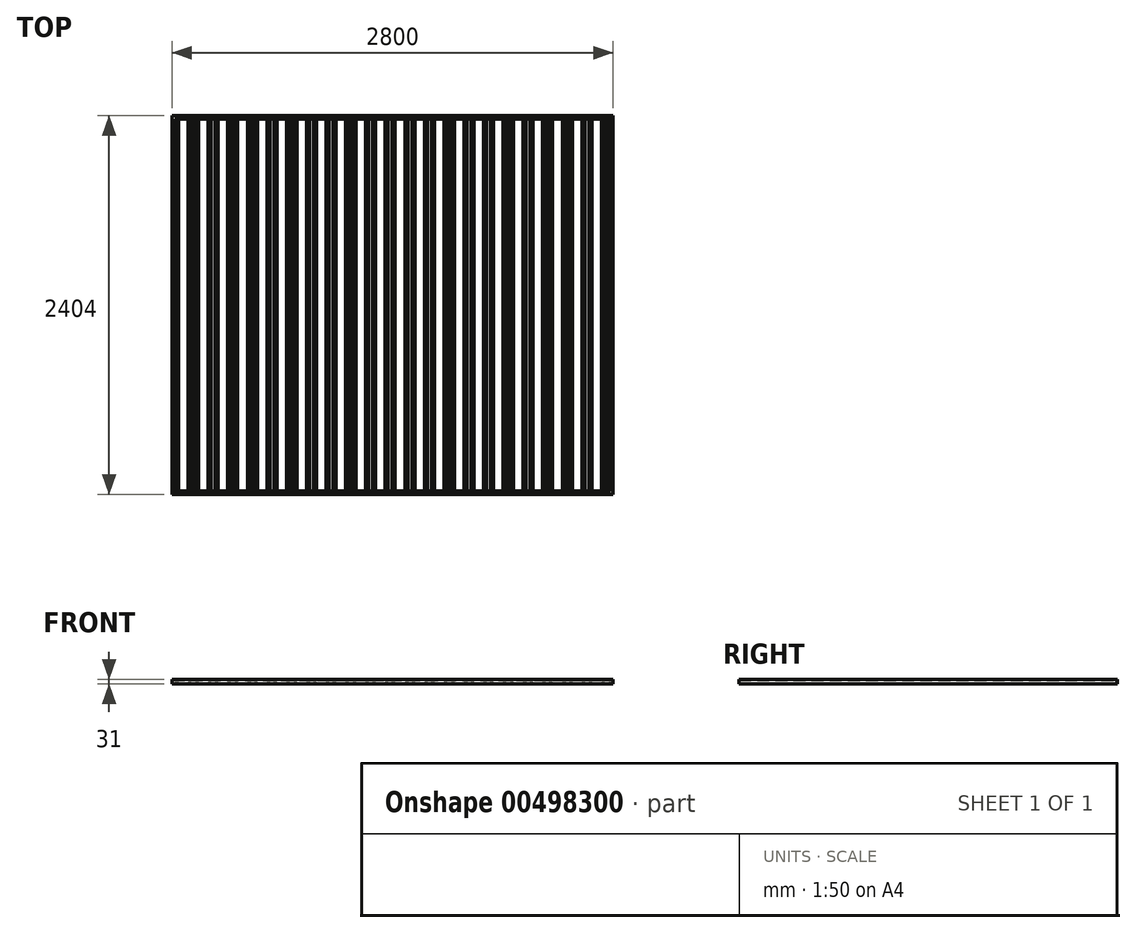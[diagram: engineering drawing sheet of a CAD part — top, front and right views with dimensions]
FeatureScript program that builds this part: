
annotation { "Feature Type Name" : "Feature", "Feature Type Description" : "" }
export const myFeature = defineFeature(function(context is Context, id is Id, definition is map)
    precondition{}
    {
        {
            var Q0;
            Q0=qCreatedBy(makeId("Front.planeOp"),FACE);
            var sketch = newSketch(context, id + "F0", { "sketchPlane" : qUnion([Q0])});
            skLineSegment(sketch, "E0", {"start": v(-64.81, 6.86) * mm, "end": v(-44.81, 6.86) * mm});
            skLineSegment(sketch, "E1", {"start": v(-44.81, 6.86) * mm, "end": v(-24.81, -13.14) * mm});
            skLineSegment(sketch, "E2", {"start": v(-24.81, -13.14) * mm, "end": v(40.19, -13.14) * mm});
            skLineSegment(sketch, "E3", {"start": v(40.19, -13.14) * mm, "end": v(60.19, 6.86) * mm});
            skLineSegment(sketch, "E4", {"start": v(60.19, 6.86) * mm, "end": v(80.19, 6.86) * mm});
            skLineSegment(sketch, "E5", {"start": v(80.19, 6.86) * mm, "end": v(100.19, -13.14) * mm});
            skLineSegment(sketch, "E6.55", {"start": v(38.12, -8.14) * mm, "end": v(58.12, 11.86) * mm});
            skLineSegment(sketch, "E6.56", {"start": v(-22.74, -8.14) * mm, "end": v(38.12, -8.14) * mm});
            skLineSegment(sketch, "E6.57", {"start": v(-42.74, 11.86) * mm, "end": v(-22.74, -8.14) * mm});
            skLineSegment(sketch, "E6.58", {"start": v(-64.81, 11.86) * mm, "end": v(-42.74, 11.86) * mm});
            skLineSegment(sketch, "E6.59", {"start": v(58.12, 11.86) * mm, "end": v(82.26, 11.86) * mm});
            skLineSegment(sketch, "E6.60", {"start": v(82.26, 11.86) * mm, "end": v(102.26, -8.14) * mm});
            skLineSegment(sketch, "E7", {"start": v(-64.81, 11.86) * mm, "end": v(-64.81, 6.86) * mm});
            skLineSegment(sketch, "E8.1.0.0", {"start": v(102.26, -8.14) * mm, "end": v(163.12, -8.14) * mm});
            skLineSegment(sketch, "E8.1.0.1", {"start": v(100.19, -13.14) * mm, "end": v(165.19, -13.14) * mm});
            skLineSegment(sketch, "E8.1.0.2", {"start": v(163.12, -8.14) * mm, "end": v(183.12, 11.86) * mm});
            skLineSegment(sketch, "E8.1.0.3", {"start": v(165.19, -13.14) * mm, "end": v(185.19, 6.86) * mm});
            skLineSegment(sketch, "E8.1.0.4", {"start": v(183.12, 11.86) * mm, "end": v(207.26, 11.86) * mm});
            skLineSegment(sketch, "E8.1.0.5", {"start": v(185.19, 6.86) * mm, "end": v(205.19, 6.86) * mm});
            skLineSegment(sketch, "E8.1.0.6", {"start": v(207.26, 11.86) * mm, "end": v(227.26, -8.14) * mm});
            skLineSegment(sketch, "E8.1.0.7", {"start": v(205.19, 6.86) * mm, "end": v(225.19, -13.14) * mm});
            skLineSegment(sketch, "E8.2.0.0", {"start": v(227.26, -8.14) * mm, "end": v(288.12, -8.14) * mm});
            skLineSegment(sketch, "E8.2.0.1", {"start": v(225.19, -13.14) * mm, "end": v(290.19, -13.14) * mm});
            skLineSegment(sketch, "E8.2.0.2", {"start": v(288.12, -8.14) * mm, "end": v(308.12, 11.86) * mm});
            skLineSegment(sketch, "E8.2.0.3", {"start": v(290.19, -13.14) * mm, "end": v(310.19, 6.86) * mm});
            skLineSegment(sketch, "E8.2.0.4", {"start": v(308.12, 11.86) * mm, "end": v(332.26, 11.86) * mm});
            skLineSegment(sketch, "E8.2.0.5", {"start": v(310.19, 6.86) * mm, "end": v(330.19, 6.86) * mm});
            skLineSegment(sketch, "E8.2.0.6", {"start": v(332.26, 11.86) * mm, "end": v(352.26, -8.14) * mm});
            skLineSegment(sketch, "E8.2.0.7", {"start": v(330.19, 6.86) * mm, "end": v(350.19, -13.14) * mm});
            skLineSegment(sketch, "E8.3.0.0", {"start": v(352.26, -8.14) * mm, "end": v(413.12, -8.14) * mm});
            skLineSegment(sketch, "E8.3.0.1", {"start": v(350.19, -13.14) * mm, "end": v(415.19, -13.14) * mm});
            skLineSegment(sketch, "E8.3.0.2", {"start": v(413.12, -8.14) * mm, "end": v(433.12, 11.86) * mm});
            skLineSegment(sketch, "E8.3.0.3", {"start": v(415.19, -13.14) * mm, "end": v(435.19, 6.86) * mm});
            skLineSegment(sketch, "E8.3.0.4", {"start": v(433.12, 11.86) * mm, "end": v(457.26, 11.86) * mm});
            skLineSegment(sketch, "E8.3.0.5", {"start": v(435.19, 6.86) * mm, "end": v(455.19, 6.86) * mm});
            skLineSegment(sketch, "E8.3.0.6", {"start": v(457.26, 11.86) * mm, "end": v(477.26, -8.14) * mm});
            skLineSegment(sketch, "E8.3.0.7", {"start": v(455.19, 6.86) * mm, "end": v(475.19, -13.14) * mm});
            skLineSegment(sketch, "E8.4.0.0", {"start": v(477.26, -8.14) * mm, "end": v(538.12, -8.14) * mm});
            skLineSegment(sketch, "E8.4.0.1", {"start": v(475.19, -13.14) * mm, "end": v(540.19, -13.14) * mm});
            skLineSegment(sketch, "E8.4.0.2", {"start": v(538.12, -8.14) * mm, "end": v(558.12, 11.86) * mm});
            skLineSegment(sketch, "E8.4.0.3", {"start": v(540.19, -13.14) * mm, "end": v(560.19, 6.86) * mm});
            skLineSegment(sketch, "E8.4.0.4", {"start": v(558.12, 11.86) * mm, "end": v(582.26, 11.86) * mm});
            skLineSegment(sketch, "E8.4.0.5", {"start": v(560.19, 6.86) * mm, "end": v(580.19, 6.86) * mm});
            skLineSegment(sketch, "E8.4.0.6", {"start": v(582.26, 11.86) * mm, "end": v(602.26, -8.14) * mm});
            skLineSegment(sketch, "E8.4.0.7", {"start": v(580.19, 6.86) * mm, "end": v(600.19, -13.14) * mm});
            skLineSegment(sketch, "E8.5.0.0", {"start": v(602.26, -8.14) * mm, "end": v(663.12, -8.14) * mm});
            skLineSegment(sketch, "E8.5.0.1", {"start": v(600.19, -13.14) * mm, "end": v(665.19, -13.14) * mm});
            skLineSegment(sketch, "E8.5.0.2", {"start": v(663.12, -8.14) * mm, "end": v(683.12, 11.86) * mm});
            skLineSegment(sketch, "E8.5.0.3", {"start": v(665.19, -13.14) * mm, "end": v(685.19, 6.86) * mm});
            skLineSegment(sketch, "E8.5.0.4", {"start": v(683.12, 11.86) * mm, "end": v(707.26, 11.86) * mm});
            skLineSegment(sketch, "E8.5.0.5", {"start": v(685.19, 6.86) * mm, "end": v(705.19, 6.86) * mm});
            skLineSegment(sketch, "E8.5.0.6", {"start": v(707.26, 11.86) * mm, "end": v(727.26, -8.14) * mm});
            skLineSegment(sketch, "E8.5.0.7", {"start": v(705.19, 6.86) * mm, "end": v(725.19, -13.14) * mm});
            skLineSegment(sketch, "E8.6.0.0", {"start": v(727.26, -8.14) * mm, "end": v(788.12, -8.14) * mm});
            skLineSegment(sketch, "E8.6.0.1", {"start": v(725.19, -13.14) * mm, "end": v(790.19, -13.14) * mm});
            skLineSegment(sketch, "E8.6.0.2", {"start": v(788.12, -8.14) * mm, "end": v(808.12, 11.86) * mm});
            skLineSegment(sketch, "E8.6.0.3", {"start": v(790.19, -13.14) * mm, "end": v(810.19, 6.86) * mm});
            skLineSegment(sketch, "E8.6.0.4", {"start": v(808.12, 11.86) * mm, "end": v(832.26, 11.86) * mm});
            skLineSegment(sketch, "E8.6.0.5", {"start": v(810.19, 6.86) * mm, "end": v(830.19, 6.86) * mm});
            skLineSegment(sketch, "E8.6.0.6", {"start": v(832.26, 11.86) * mm, "end": v(852.26, -8.14) * mm});
            skLineSegment(sketch, "E8.6.0.7", {"start": v(830.19, 6.86) * mm, "end": v(850.19, -13.14) * mm});
            skLineSegment(sketch, "E8.7.0.0", {"start": v(852.26, -8.14) * mm, "end": v(913.12, -8.14) * mm});
            skLineSegment(sketch, "E8.7.0.1", {"start": v(850.19, -13.14) * mm, "end": v(915.19, -13.14) * mm});
            skLineSegment(sketch, "E8.7.0.2", {"start": v(913.12, -8.14) * mm, "end": v(933.12, 11.86) * mm});
            skLineSegment(sketch, "E8.7.0.3", {"start": v(915.19, -13.14) * mm, "end": v(935.19, 6.86) * mm});
            skLineSegment(sketch, "E8.7.0.4", {"start": v(933.12, 11.86) * mm, "end": v(957.26, 11.86) * mm});
            skLineSegment(sketch, "E8.7.0.5", {"start": v(935.19, 6.86) * mm, "end": v(955.19, 6.86) * mm});
            skLineSegment(sketch, "E8.7.0.6", {"start": v(957.26, 11.86) * mm, "end": v(977.26, -8.14) * mm});
            skLineSegment(sketch, "E8.7.0.7", {"start": v(955.19, 6.86) * mm, "end": v(975.19, -13.14) * mm});
            skLineSegment(sketch, "E8.8.0.0", {"start": v(977.26, -8.14) * mm, "end": v(1038.12, -8.14) * mm});
            skLineSegment(sketch, "E8.8.0.1", {"start": v(975.19, -13.14) * mm, "end": v(1040.19, -13.14) * mm});
            skLineSegment(sketch, "E8.8.0.2", {"start": v(1038.12, -8.14) * mm, "end": v(1058.12, 11.86) * mm});
            skLineSegment(sketch, "E8.8.0.3", {"start": v(1040.19, -13.14) * mm, "end": v(1060.19, 6.86) * mm});
            skLineSegment(sketch, "E8.8.0.4", {"start": v(1058.12, 11.86) * mm, "end": v(1082.26, 11.86) * mm});
            skLineSegment(sketch, "E8.8.0.5", {"start": v(1060.19, 6.86) * mm, "end": v(1080.19, 6.86) * mm});
            skLineSegment(sketch, "E8.8.0.6", {"start": v(1082.26, 11.86) * mm, "end": v(1102.26, -8.14) * mm});
            skLineSegment(sketch, "E8.8.0.7", {"start": v(1080.19, 6.86) * mm, "end": v(1100.19, -13.14) * mm});
            skLineSegment(sketch, "E8.9.0.0", {"start": v(1102.26, -8.14) * mm, "end": v(1163.12, -8.14) * mm});
            skLineSegment(sketch, "E8.9.0.1", {"start": v(1100.19, -13.14) * mm, "end": v(1165.19, -13.14) * mm});
            skLineSegment(sketch, "E8.9.0.2", {"start": v(1163.12, -8.14) * mm, "end": v(1183.12, 11.86) * mm});
            skLineSegment(sketch, "E8.9.0.3", {"start": v(1165.19, -13.14) * mm, "end": v(1185.19, 6.86) * mm});
            skLineSegment(sketch, "E8.9.0.4", {"start": v(1183.12, 11.86) * mm, "end": v(1207.26, 11.86) * mm});
            skLineSegment(sketch, "E8.9.0.5", {"start": v(1185.19, 6.86) * mm, "end": v(1205.19, 6.86) * mm});
            skLineSegment(sketch, "E8.9.0.6", {"start": v(1207.26, 11.86) * mm, "end": v(1227.26, -8.14) * mm});
            skLineSegment(sketch, "E8.9.0.7", {"start": v(1205.19, 6.86) * mm, "end": v(1225.19, -13.14) * mm});
            skLineSegment(sketch, "E8.10.0.0", {"start": v(1227.26, -8.14) * mm, "end": v(1288.12, -8.14) * mm});
            skLineSegment(sketch, "E8.10.0.1", {"start": v(1225.19, -13.14) * mm, "end": v(1290.19, -13.14) * mm});
            skLineSegment(sketch, "E8.10.0.2", {"start": v(1288.12, -8.14) * mm, "end": v(1308.12, 11.86) * mm});
            skLineSegment(sketch, "E8.10.0.3", {"start": v(1290.19, -13.14) * mm, "end": v(1310.19, 6.86) * mm});
            skLineSegment(sketch, "E8.10.0.4", {"start": v(1308.12, 11.86) * mm, "end": v(1332.26, 11.86) * mm});
            skLineSegment(sketch, "E8.10.0.5", {"start": v(1310.19, 6.86) * mm, "end": v(1330.19, 6.86) * mm});
            skLineSegment(sketch, "E8.10.0.6", {"start": v(1332.26, 11.86) * mm, "end": v(1352.26, -8.14) * mm});
            skLineSegment(sketch, "E8.10.0.7", {"start": v(1330.19, 6.86) * mm, "end": v(1350.19, -13.14) * mm});
            skLineSegment(sketch, "E8.11.0.0", {"start": v(1352.26, -8.14) * mm, "end": v(1413.12, -8.14) * mm});
            skLineSegment(sketch, "E8.11.0.1", {"start": v(1350.19, -13.14) * mm, "end": v(1415.19, -13.14) * mm});
            skLineSegment(sketch, "E8.11.0.2", {"start": v(1413.12, -8.14) * mm, "end": v(1433.12, 11.86) * mm});
            skLineSegment(sketch, "E8.11.0.3", {"start": v(1415.19, -13.14) * mm, "end": v(1435.19, 6.86) * mm});
            skLineSegment(sketch, "E8.11.0.4", {"start": v(1433.12, 11.86) * mm, "end": v(1457.26, 11.86) * mm});
            skLineSegment(sketch, "E8.11.0.5", {"start": v(1435.19, 6.86) * mm, "end": v(1455.19, 6.86) * mm});
            skLineSegment(sketch, "E8.11.0.6", {"start": v(1457.26, 11.86) * mm, "end": v(1477.26, -8.14) * mm});
            skLineSegment(sketch, "E8.11.0.7", {"start": v(1455.19, 6.86) * mm, "end": v(1475.19, -13.14) * mm});
            skLineSegment(sketch, "E8.12.0.0", {"start": v(1477.26, -8.14) * mm, "end": v(1538.12, -8.14) * mm});
            skLineSegment(sketch, "E8.12.0.1", {"start": v(1475.19, -13.14) * mm, "end": v(1540.19, -13.14) * mm});
            skLineSegment(sketch, "E8.12.0.2", {"start": v(1538.12, -8.14) * mm, "end": v(1558.12, 11.86) * mm});
            skLineSegment(sketch, "E8.12.0.3", {"start": v(1540.19, -13.14) * mm, "end": v(1560.19, 6.86) * mm});
            skLineSegment(sketch, "E8.12.0.4", {"start": v(1558.12, 11.86) * mm, "end": v(1582.26, 11.86) * mm});
            skLineSegment(sketch, "E8.12.0.5", {"start": v(1560.19, 6.86) * mm, "end": v(1580.19, 6.86) * mm});
            skLineSegment(sketch, "E8.12.0.6", {"start": v(1582.26, 11.86) * mm, "end": v(1602.26, -8.14) * mm});
            skLineSegment(sketch, "E8.12.0.7", {"start": v(1580.19, 6.86) * mm, "end": v(1600.19, -13.14) * mm});
            skLineSegment(sketch, "E8.13.0.0", {"start": v(1602.26, -8.14) * mm, "end": v(1663.12, -8.14) * mm});
            skLineSegment(sketch, "E8.13.0.1", {"start": v(1600.19, -13.14) * mm, "end": v(1665.19, -13.14) * mm});
            skLineSegment(sketch, "E8.13.0.2", {"start": v(1663.12, -8.14) * mm, "end": v(1683.12, 11.86) * mm});
            skLineSegment(sketch, "E8.13.0.3", {"start": v(1665.19, -13.14) * mm, "end": v(1685.19, 6.86) * mm});
            skLineSegment(sketch, "E8.13.0.4", {"start": v(1683.12, 11.86) * mm, "end": v(1707.26, 11.86) * mm});
            skLineSegment(sketch, "E8.13.0.5", {"start": v(1685.19, 6.86) * mm, "end": v(1705.19, 6.86) * mm});
            skLineSegment(sketch, "E8.13.0.6", {"start": v(1707.26, 11.86) * mm, "end": v(1727.26, -8.14) * mm});
            skLineSegment(sketch, "E8.13.0.7", {"start": v(1705.19, 6.86) * mm, "end": v(1725.19, -13.14) * mm});
            skLineSegment(sketch, "E8.14.0.0", {"start": v(1727.26, -8.14) * mm, "end": v(1788.12, -8.14) * mm});
            skLineSegment(sketch, "E8.14.0.1", {"start": v(1725.19, -13.14) * mm, "end": v(1790.19, -13.14) * mm});
            skLineSegment(sketch, "E8.14.0.2", {"start": v(1788.12, -8.14) * mm, "end": v(1808.12, 11.86) * mm});
            skLineSegment(sketch, "E8.14.0.3", {"start": v(1790.19, -13.14) * mm, "end": v(1810.19, 6.86) * mm});
            skLineSegment(sketch, "E8.14.0.4", {"start": v(1808.12, 11.86) * mm, "end": v(1832.26, 11.86) * mm});
            skLineSegment(sketch, "E8.14.0.5", {"start": v(1810.19, 6.86) * mm, "end": v(1830.19, 6.86) * mm});
            skLineSegment(sketch, "E8.14.0.6", {"start": v(1832.26, 11.86) * mm, "end": v(1852.26, -8.14) * mm});
            skLineSegment(sketch, "E8.14.0.7", {"start": v(1830.19, 6.86) * mm, "end": v(1850.19, -13.14) * mm});
            skLineSegment(sketch, "E8.15.0.0", {"start": v(1852.26, -8.14) * mm, "end": v(1913.12, -8.14) * mm});
            skLineSegment(sketch, "E8.15.0.1", {"start": v(1850.19, -13.14) * mm, "end": v(1915.19, -13.14) * mm});
            skLineSegment(sketch, "E8.15.0.2", {"start": v(1913.12, -8.14) * mm, "end": v(1933.12, 11.86) * mm});
            skLineSegment(sketch, "E8.15.0.3", {"start": v(1915.19, -13.14) * mm, "end": v(1935.19, 6.86) * mm});
            skLineSegment(sketch, "E8.15.0.4", {"start": v(1933.12, 11.86) * mm, "end": v(1957.26, 11.86) * mm});
            skLineSegment(sketch, "E8.15.0.5", {"start": v(1935.19, 6.86) * mm, "end": v(1955.19, 6.86) * mm});
            skLineSegment(sketch, "E8.15.0.6", {"start": v(1957.26, 11.86) * mm, "end": v(1977.26, -8.14) * mm});
            skLineSegment(sketch, "E8.15.0.7", {"start": v(1955.19, 6.86) * mm, "end": v(1975.19, -13.14) * mm});
            skLineSegment(sketch, "E8.16.0.0", {"start": v(1977.26, -8.14) * mm, "end": v(2038.12, -8.14) * mm});
            skLineSegment(sketch, "E8.16.0.1", {"start": v(1975.19, -13.14) * mm, "end": v(2040.19, -13.14) * mm});
            skLineSegment(sketch, "E8.16.0.2", {"start": v(2038.12, -8.14) * mm, "end": v(2058.12, 11.86) * mm});
            skLineSegment(sketch, "E8.16.0.3", {"start": v(2040.19, -13.14) * mm, "end": v(2060.19, 6.86) * mm});
            skLineSegment(sketch, "E8.16.0.4", {"start": v(2058.12, 11.86) * mm, "end": v(2082.26, 11.86) * mm});
            skLineSegment(sketch, "E8.16.0.5", {"start": v(2060.19, 6.86) * mm, "end": v(2080.19, 6.86) * mm});
            skLineSegment(sketch, "E8.16.0.6", {"start": v(2082.26, 11.86) * mm, "end": v(2102.26, -8.14) * mm});
            skLineSegment(sketch, "E8.16.0.7", {"start": v(2080.19, 6.86) * mm, "end": v(2100.19, -13.14) * mm});
            skLineSegment(sketch, "E8.17.0.0", {"start": v(2102.26, -8.14) * mm, "end": v(2163.12, -8.14) * mm});
            skLineSegment(sketch, "E8.17.0.1", {"start": v(2100.19, -13.14) * mm, "end": v(2165.19, -13.14) * mm});
            skLineSegment(sketch, "E8.17.0.2", {"start": v(2163.12, -8.14) * mm, "end": v(2183.12, 11.86) * mm});
            skLineSegment(sketch, "E8.17.0.3", {"start": v(2165.19, -13.14) * mm, "end": v(2185.19, 6.86) * mm});
            skLineSegment(sketch, "E8.17.0.4", {"start": v(2183.12, 11.86) * mm, "end": v(2207.26, 11.86) * mm});
            skLineSegment(sketch, "E8.17.0.5", {"start": v(2185.19, 6.86) * mm, "end": v(2205.19, 6.86) * mm});
            skLineSegment(sketch, "E8.17.0.6", {"start": v(2207.26, 11.86) * mm, "end": v(2227.26, -8.14) * mm});
            skLineSegment(sketch, "E8.17.0.7", {"start": v(2205.19, 6.86) * mm, "end": v(2225.19, -13.14) * mm});
            skLineSegment(sketch, "E8.18.0.0", {"start": v(2227.26, -8.14) * mm, "end": v(2288.12, -8.14) * mm});
            skLineSegment(sketch, "E8.18.0.1", {"start": v(2225.19, -13.14) * mm, "end": v(2290.19, -13.14) * mm});
            skLineSegment(sketch, "E8.18.0.2", {"start": v(2288.12, -8.14) * mm, "end": v(2308.12, 11.86) * mm});
            skLineSegment(sketch, "E8.18.0.3", {"start": v(2290.19, -13.14) * mm, "end": v(2310.19, 6.86) * mm});
            skLineSegment(sketch, "E8.18.0.4", {"start": v(2308.12, 11.86) * mm, "end": v(2332.26, 11.86) * mm});
            skLineSegment(sketch, "E8.18.0.5", {"start": v(2310.19, 6.86) * mm, "end": v(2330.19, 6.86) * mm});
            skLineSegment(sketch, "E8.18.0.6", {"start": v(2332.26, 11.86) * mm, "end": v(2352.26, -8.14) * mm});
            skLineSegment(sketch, "E8.18.0.7", {"start": v(2330.19, 6.86) * mm, "end": v(2350.19, -13.14) * mm});
            skLineSegment(sketch, "E8.19.0.0", {"start": v(2352.26, -8.14) * mm, "end": v(2413.12, -8.14) * mm});
            skLineSegment(sketch, "E8.19.0.1", {"start": v(2350.19, -13.14) * mm, "end": v(2415.19, -13.14) * mm});
            skLineSegment(sketch, "E8.19.0.2", {"start": v(2413.12, -8.14) * mm, "end": v(2433.12, 11.86) * mm});
            skLineSegment(sketch, "E8.19.0.3", {"start": v(2415.19, -13.14) * mm, "end": v(2435.19, 6.86) * mm});
            skLineSegment(sketch, "E8.19.0.4", {"start": v(2433.12, 11.86) * mm, "end": v(2457.26, 11.86) * mm});
            skLineSegment(sketch, "E8.19.0.5", {"start": v(2435.19, 6.86) * mm, "end": v(2455.19, 6.86) * mm});
            skLineSegment(sketch, "E8.19.0.6", {"start": v(2457.26, 11.86) * mm, "end": v(2477.26, -8.14) * mm});
            skLineSegment(sketch, "E8.19.0.7", {"start": v(2455.19, 6.86) * mm, "end": v(2475.19, -13.14) * mm});
            skLineSegment(sketch, "E8.20.0.0", {"start": v(2477.26, -8.14) * mm, "end": v(2538.12, -8.14) * mm});
            skLineSegment(sketch, "E8.20.0.1", {"start": v(2475.19, -13.14) * mm, "end": v(2540.19, -13.14) * mm});
            skLineSegment(sketch, "E8.20.0.2", {"start": v(2538.12, -8.14) * mm, "end": v(2558.12, 11.86) * mm});
            skLineSegment(sketch, "E8.20.0.3", {"start": v(2540.19, -13.14) * mm, "end": v(2560.19, 6.86) * mm});
            skLineSegment(sketch, "E8.20.0.4", {"start": v(2558.12, 11.86) * mm, "end": v(2582.26, 11.86) * mm});
            skLineSegment(sketch, "E8.20.0.5", {"start": v(2560.19, 6.86) * mm, "end": v(2580.19, 6.86) * mm});
            skLineSegment(sketch, "E8.20.0.6", {"start": v(2582.26, 11.86) * mm, "end": v(2602.26, -8.14) * mm});
            skLineSegment(sketch, "E8.20.0.7", {"start": v(2580.19, 6.86) * mm, "end": v(2600.19, -13.14) * mm});
            skLineSegment(sketch, "E8.21.0.0", {"start": v(2602.26, -8.14) * mm, "end": v(2663.12, -8.14) * mm});
            skLineSegment(sketch, "E8.21.0.1", {"start": v(2600.19, -13.14) * mm, "end": v(2665.19, -13.14) * mm});
            skLineSegment(sketch, "E8.21.0.2", {"start": v(2663.12, -8.14) * mm, "end": v(2683.12, 11.86) * mm});
            skLineSegment(sketch, "E8.21.0.3", {"start": v(2665.19, -13.14) * mm, "end": v(2685.19, 6.86) * mm});
            skLineSegment(sketch, "E8.21.0.4", {"start": v(2683.12, 11.86) * mm, "end": v(2707.26, 11.86) * mm});
            skLineSegment(sketch, "E8.21.0.5", {"start": v(2685.19, 6.86) * mm, "end": v(2705.19, 6.86) * mm});
            skLineSegment(sketch, "E8.21.0.6", {"start": v(2707.26, 11.86) * mm, "end": v(2727.26, -8.14) * mm});
            skLineSegment(sketch, "E8.21.0.7", {"start": v(2705.19, 6.86) * mm, "end": v(2725.19, -13.14) * mm});
            skLineSegment(sketch, "E8.direction1", {"start": v(-22.74, -8.14) * mm, "end": v(102.26, -8.14) * mm, "construction": true});
            skLineSegment(sketch, "E9", {"start": v(2727.26, -8.14) * mm, "end": v(2725.19, -13.14) * mm});
            skSolve(sketch);
        }
        {
            var Q0;
            Q0=qCreatedBy(makeId("Right.planeOp"),FACE);
            var sketch = newSketch(context, id + "F1", { "sketchPlane" : qUnion([Q0])});
            skLineSegment(sketch, "E10", {"start": v(0, 11.86) * mm, "end": v(2400, 11.86) * mm});
            skSolve(sketch);
        }
        {
            var Q0;
            Q0=makeQuery(id+"F0.imprint","IMPRINT",FACE,{"disambiguationData":[TD([[makeQuery(id+"F0.imprint","IMPRINT",EDGE,{"derivedFrom":sQuery(id+"F0.wireOp",EDGE,"E0")}),1.0]])]});
            var Q1;
            Q1=sQuery(id+"F1.wireOp",EDGE,"E10");
            sweep(context, id + "F2", {"profiles" : qUnion([Q0]), "path" : qUnion([Q1])});
        }
        {
            var Q0;
            Q0=makeQuery(id+"F2.opSweep","SWEPT_FACE",FACE,{"disambiguationData":[OSD([sQuery(id+"F0.wireOp",EDGE,"E7"),sQuery(id+"F1.wireOp",EDGE,"E10")])]});
            var sketch = newSketch(context, id + "F3", { "sketchPlane" : qUnion([Q0])});
            skLineSegment(sketch, "E11", {"start": v(-17.89, 12.86) * mm, "end": v(-1, 12.86) * mm});
            skLineSegment(sketch, "E12", {"start": v(-1, 12.86) * mm, "end": v(-1, -14.14) * mm});
            skLineSegment(sketch, "E13", {"start": v(-1, -14.14) * mm, "end": v(-18, -14.14) * mm});
            skLineSegment(sketch, "E14", {"start": v(-18, -14.14) * mm, "end": v(-18, -16.14) * mm});
            skLineSegment(sketch, "E15", {"start": v(-18, -16.14) * mm, "end": v(2, -16.14) * mm});
            skLineSegment(sketch, "E16", {"start": v(2, -16.14) * mm, "end": v(2, 14.86) * mm});
            skLineSegment(sketch, "E17", {"start": v(2, 14.86) * mm, "end": v(-18, 14.86) * mm});
            skLineSegment(sketch, "E18", {"start": v(-18, 14.86) * mm, "end": v(-17.89, 12.86) * mm});
            skSolve(sketch);
        }
        {
            var Q0;
            Q0=makeQuery(id+"F3.imprint","IMPRINT",FACE,{"disambiguationData":[TD([[makeQuery(id+"F3.imprint","IMPRINT",EDGE,{"derivedFrom":sQuery(id+"F3.wireOp",EDGE,"E11")}),1.0]])]});
            var Q1;
            Q1=makeQuery(id+"F2.opSweep","SWEPT_FACE",FACE,{"disambiguationData":[OSD([sQuery(id+"F0.wireOp",EDGE,"E9"),sQuery(id+"F1.wireOp",EDGE,"E10")])]});
            extrude(context, id + "F4", {"entities" : qUnion([Q0]), "oppositeDirection" : true, "endBoundEntityFace" : qUnion([Q1]), "depth" : 2800 * mm});
        }
        {
            var Q0;
            Q0=makeQuery(id+"F2.opSweep","CAP_FACE",FACE,{"disambiguationData":[OSD([sQuery(id+"F0.wireOp",EDGE,"E0"),sQuery(id+"F0.wireOp",EDGE,"E1"),sQuery(id+"F0.wireOp",EDGE,"E2"),sQuery(id+"F0.wireOp",EDGE,"E3"),sQuery(id+"F0.wireOp",EDGE,"E4"),sQuery(id+"F0.wireOp",EDGE,"E5"),sQuery(id+"F0.wireOp",EDGE,"E6.55"),sQuery(id+"F0.wireOp",EDGE,"E6.56"),sQuery(id+"F0.wireOp",EDGE,"E6.57"),sQuery(id+"F0.wireOp",EDGE,"E6.58"),sQuery(id+"F0.wireOp",EDGE,"E6.59"),sQuery(id+"F0.wireOp",EDGE,"E6.60"),sQuery(id+"F0.wireOp",EDGE,"E7"),sQuery(id+"F0.wireOp",EDGE,"E8.1.0.0"),sQuery(id+"F0.wireOp",EDGE,"E8.1.0.1"),sQuery(id+"F0.wireOp",EDGE,"E8.1.0.2"),sQuery(id+"F0.wireOp",EDGE,"E8.1.0.3"),sQuery(id+"F0.wireOp",EDGE,"E8.1.0.4"),sQuery(id+"F0.wireOp",EDGE,"E8.1.0.5"),sQuery(id+"F0.wireOp",EDGE,"E8.1.0.6"),sQuery(id+"F0.wireOp",EDGE,"E8.1.0.7"),sQuery(id+"F0.wireOp",EDGE,"E8.2.0.0"),sQuery(id+"F0.wireOp",EDGE,"E8.2.0.1"),sQuery(id+"F0.wireOp",EDGE,"E8.2.0.2"),sQuery(id+"F0.wireOp",EDGE,"E8.2.0.3"),sQuery(id+"F0.wireOp",EDGE,"E8.2.0.4"),sQuery(id+"F0.wireOp",EDGE,"E8.2.0.5"),sQuery(id+"F0.wireOp",EDGE,"E8.2.0.6"),sQuery(id+"F0.wireOp",EDGE,"E8.2.0.7"),sQuery(id+"F0.wireOp",EDGE,"E8.3.0.0"),sQuery(id+"F0.wireOp",EDGE,"E8.3.0.1"),sQuery(id+"F0.wireOp",EDGE,"E8.3.0.2"),sQuery(id+"F0.wireOp",EDGE,"E8.3.0.3"),sQuery(id+"F0.wireOp",EDGE,"E8.3.0.4"),sQuery(id+"F0.wireOp",EDGE,"E8.3.0.5"),sQuery(id+"F0.wireOp",EDGE,"E8.3.0.6"),sQuery(id+"F0.wireOp",EDGE,"E8.3.0.7"),sQuery(id+"F0.wireOp",EDGE,"E8.4.0.0"),sQuery(id+"F0.wireOp",EDGE,"E8.4.0.1"),sQuery(id+"F0.wireOp",EDGE,"E8.4.0.2"),sQuery(id+"F0.wireOp",EDGE,"E8.4.0.3"),sQuery(id+"F0.wireOp",EDGE,"E8.4.0.4"),sQuery(id+"F0.wireOp",EDGE,"E8.4.0.5"),sQuery(id+"F0.wireOp",EDGE,"E8.4.0.6"),sQuery(id+"F0.wireOp",EDGE,"E8.4.0.7"),sQuery(id+"F0.wireOp",EDGE,"E8.5.0.0"),sQuery(id+"F0.wireOp",EDGE,"E8.5.0.1"),sQuery(id+"F0.wireOp",EDGE,"E8.5.0.2"),sQuery(id+"F0.wireOp",EDGE,"E8.5.0.3"),sQuery(id+"F0.wireOp",EDGE,"E8.5.0.4"),sQuery(id+"F0.wireOp",EDGE,"E8.5.0.5"),sQuery(id+"F0.wireOp",EDGE,"E8.5.0.6"),sQuery(id+"F0.wireOp",EDGE,"E8.5.0.7"),sQuery(id+"F0.wireOp",EDGE,"E8.6.0.0"),sQuery(id+"F0.wireOp",EDGE,"E8.6.0.1"),sQuery(id+"F0.wireOp",EDGE,"E8.6.0.2"),sQuery(id+"F0.wireOp",EDGE,"E8.6.0.3"),sQuery(id+"F0.wireOp",EDGE,"E8.6.0.4"),sQuery(id+"F0.wireOp",EDGE,"E8.6.0.5"),sQuery(id+"F0.wireOp",EDGE,"E8.6.0.6"),sQuery(id+"F0.wireOp",EDGE,"E8.6.0.7"),sQuery(id+"F0.wireOp",EDGE,"E8.7.0.0"),sQuery(id+"F0.wireOp",EDGE,"E8.7.0.1"),sQuery(id+"F0.wireOp",EDGE,"E8.7.0.2"),sQuery(id+"F0.wireOp",EDGE,"E8.7.0.3"),sQuery(id+"F0.wireOp",EDGE,"E8.7.0.4"),sQuery(id+"F0.wireOp",EDGE,"E8.7.0.5"),sQuery(id+"F0.wireOp",EDGE,"E8.7.0.6"),sQuery(id+"F0.wireOp",EDGE,"E8.7.0.7"),sQuery(id+"F0.wireOp",EDGE,"E8.8.0.0"),sQuery(id+"F0.wireOp",EDGE,"E8.8.0.1"),sQuery(id+"F0.wireOp",EDGE,"E8.8.0.2"),sQuery(id+"F0.wireOp",EDGE,"E8.8.0.3"),sQuery(id+"F0.wireOp",EDGE,"E8.8.0.4"),sQuery(id+"F0.wireOp",EDGE,"E8.8.0.5"),sQuery(id+"F0.wireOp",EDGE,"E8.8.0.6"),sQuery(id+"F0.wireOp",EDGE,"E8.8.0.7"),sQuery(id+"F0.wireOp",EDGE,"E8.9.0.0"),sQuery(id+"F0.wireOp",EDGE,"E8.9.0.1"),sQuery(id+"F0.wireOp",EDGE,"E8.9.0.2"),sQuery(id+"F0.wireOp",EDGE,"E8.9.0.3"),sQuery(id+"F0.wireOp",EDGE,"E8.9.0.4"),sQuery(id+"F0.wireOp",EDGE,"E8.9.0.5"),sQuery(id+"F0.wireOp",EDGE,"E8.9.0.6"),sQuery(id+"F0.wireOp",EDGE,"E8.9.0.7"),sQuery(id+"F0.wireOp",EDGE,"E8.10.0.0"),sQuery(id+"F0.wireOp",EDGE,"E8.10.0.1"),sQuery(id+"F0.wireOp",EDGE,"E8.10.0.2"),sQuery(id+"F0.wireOp",EDGE,"E8.10.0.3"),sQuery(id+"F0.wireOp",EDGE,"E8.10.0.4"),sQuery(id+"F0.wireOp",EDGE,"E8.10.0.5"),sQuery(id+"F0.wireOp",EDGE,"E8.10.0.6"),sQuery(id+"F0.wireOp",EDGE,"E8.10.0.7"),sQuery(id+"F0.wireOp",EDGE,"E8.11.0.0"),sQuery(id+"F0.wireOp",EDGE,"E8.11.0.1"),sQuery(id+"F0.wireOp",EDGE,"E8.11.0.2"),sQuery(id+"F0.wireOp",EDGE,"E8.11.0.3"),sQuery(id+"F0.wireOp",EDGE,"E8.11.0.4"),sQuery(id+"F0.wireOp",EDGE,"E8.11.0.5"),sQuery(id+"F0.wireOp",EDGE,"E8.11.0.6"),sQuery(id+"F0.wireOp",EDGE,"E8.11.0.7"),sQuery(id+"F0.wireOp",EDGE,"E8.12.0.0"),sQuery(id+"F0.wireOp",EDGE,"E8.12.0.1"),sQuery(id+"F0.wireOp",EDGE,"E8.12.0.2"),sQuery(id+"F0.wireOp",EDGE,"E8.12.0.3"),sQuery(id+"F0.wireOp",EDGE,"E8.12.0.4"),sQuery(id+"F0.wireOp",EDGE,"E8.12.0.5"),sQuery(id+"F0.wireOp",EDGE,"E8.12.0.6"),sQuery(id+"F0.wireOp",EDGE,"E8.12.0.7"),sQuery(id+"F0.wireOp",EDGE,"E8.13.0.0"),sQuery(id+"F0.wireOp",EDGE,"E8.13.0.1"),sQuery(id+"F0.wireOp",EDGE,"E8.13.0.2"),sQuery(id+"F0.wireOp",EDGE,"E8.13.0.3"),sQuery(id+"F0.wireOp",EDGE,"E8.13.0.4"),sQuery(id+"F0.wireOp",EDGE,"E8.13.0.5"),sQuery(id+"F0.wireOp",EDGE,"E8.13.0.6"),sQuery(id+"F0.wireOp",EDGE,"E8.13.0.7"),sQuery(id+"F0.wireOp",EDGE,"E8.14.0.0"),sQuery(id+"F0.wireOp",EDGE,"E8.14.0.1"),sQuery(id+"F0.wireOp",EDGE,"E8.14.0.2"),sQuery(id+"F0.wireOp",EDGE,"E8.14.0.3"),sQuery(id+"F0.wireOp",EDGE,"E8.14.0.4"),sQuery(id+"F0.wireOp",EDGE,"E8.14.0.5"),sQuery(id+"F0.wireOp",EDGE,"E8.14.0.6"),sQuery(id+"F0.wireOp",EDGE,"E8.14.0.7"),sQuery(id+"F0.wireOp",EDGE,"E8.15.0.0"),sQuery(id+"F0.wireOp",EDGE,"E8.15.0.1"),sQuery(id+"F0.wireOp",EDGE,"E8.15.0.2"),sQuery(id+"F0.wireOp",EDGE,"E8.15.0.3"),sQuery(id+"F0.wireOp",EDGE,"E8.15.0.4"),sQuery(id+"F0.wireOp",EDGE,"E8.15.0.5"),sQuery(id+"F0.wireOp",EDGE,"E8.15.0.6"),sQuery(id+"F0.wireOp",EDGE,"E8.15.0.7"),sQuery(id+"F0.wireOp",EDGE,"E8.16.0.0"),sQuery(id+"F0.wireOp",EDGE,"E8.16.0.1"),sQuery(id+"F0.wireOp",EDGE,"E8.16.0.2"),sQuery(id+"F0.wireOp",EDGE,"E8.16.0.3"),sQuery(id+"F0.wireOp",EDGE,"E8.16.0.4"),sQuery(id+"F0.wireOp",EDGE,"E8.16.0.5"),sQuery(id+"F0.wireOp",EDGE,"E8.16.0.6"),sQuery(id+"F0.wireOp",EDGE,"E8.16.0.7"),sQuery(id+"F0.wireOp",EDGE,"E8.17.0.0"),sQuery(id+"F0.wireOp",EDGE,"E8.17.0.1"),sQuery(id+"F0.wireOp",EDGE,"E8.17.0.2"),sQuery(id+"F0.wireOp",EDGE,"E8.17.0.3"),sQuery(id+"F0.wireOp",EDGE,"E8.17.0.4"),sQuery(id+"F0.wireOp",EDGE,"E8.17.0.5"),sQuery(id+"F0.wireOp",EDGE,"E8.17.0.6"),sQuery(id+"F0.wireOp",EDGE,"E8.17.0.7"),sQuery(id+"F0.wireOp",EDGE,"E8.18.0.0"),sQuery(id+"F0.wireOp",EDGE,"E8.18.0.1"),sQuery(id+"F0.wireOp",EDGE,"E8.18.0.2"),sQuery(id+"F0.wireOp",EDGE,"E8.18.0.3"),sQuery(id+"F0.wireOp",EDGE,"E8.18.0.4"),sQuery(id+"F0.wireOp",EDGE,"E8.18.0.5"),sQuery(id+"F0.wireOp",EDGE,"E8.18.0.6"),sQuery(id+"F0.wireOp",EDGE,"E8.18.0.7"),sQuery(id+"F0.wireOp",EDGE,"E8.19.0.0"),sQuery(id+"F0.wireOp",EDGE,"E8.19.0.1"),sQuery(id+"F0.wireOp",EDGE,"E8.19.0.2"),sQuery(id+"F0.wireOp",EDGE,"E8.19.0.3"),sQuery(id+"F0.wireOp",EDGE,"E8.19.0.4"),sQuery(id+"F0.wireOp",EDGE,"E8.19.0.5"),sQuery(id+"F0.wireOp",EDGE,"E8.19.0.6"),sQuery(id+"F0.wireOp",EDGE,"E8.19.0.7"),sQuery(id+"F0.wireOp",EDGE,"E8.20.0.0"),sQuery(id+"F0.wireOp",EDGE,"E8.20.0.1"),sQuery(id+"F0.wireOp",EDGE,"E8.20.0.2"),sQuery(id+"F0.wireOp",EDGE,"E8.20.0.3"),sQuery(id+"F0.wireOp",EDGE,"E8.20.0.4"),sQuery(id+"F0.wireOp",EDGE,"E8.20.0.5"),sQuery(id+"F0.wireOp",EDGE,"E8.20.0.6"),sQuery(id+"F0.wireOp",EDGE,"E8.20.0.7"),sQuery(id+"F0.wireOp",EDGE,"E8.21.0.0"),sQuery(id+"F0.wireOp",EDGE,"E8.21.0.1"),sQuery(id+"F0.wireOp",EDGE,"E8.21.0.2"),sQuery(id+"F0.wireOp",EDGE,"E8.21.0.3"),sQuery(id+"F0.wireOp",EDGE,"E8.21.0.4"),sQuery(id+"F0.wireOp",EDGE,"E8.21.0.5"),sQuery(id+"F0.wireOp",EDGE,"E8.21.0.6"),sQuery(id+"F0.wireOp",EDGE,"E8.21.0.7"),sQuery(id+"F0.wireOp",EDGE,"E9"),sQuery(id+"F1.wireOp",VERTEX,"E10.start")])],"isStart":true});
            cPlane(context, id + "F5", {"entities" : qUnion([Q0]), "cplaneType" : CPlaneType.OFFSET, "offset" : 1200 * mm, "oppositeDirection" : true, "width" : 150 * mm, "height" : 150 * mm});
        }
        {
            var Q0;
            Q0=makeQuery(id+"F4.opExtrude","SWEPT_FACE",FACE,{"disambiguationData":[OSD([sQuery(id+"F3.wireOp",EDGE,"E16")])]});
            var sketch = newSketch(context, id + "F6", { "sketchPlane" : qUnion([Q0])});
            skLineSegment(sketch, "E19.bottom", {"start": v(2735.19, 14.86) * mm, "end": v(2715.19, 14.86) * mm});
            skLineSegment(sketch, "E19.top", {"start": v(2735.19, -16.14) * mm, "end": v(2715.19, -16.14) * mm});
            skLineSegment(sketch, "E19.left", {"start": v(2735.19, 14.86) * mm, "end": v(2735.19, -16.14) * mm});
            skLineSegment(sketch, "E19.right", {"start": v(2715.19, 14.86) * mm, "end": v(2715.19, 12.86) * mm});
            skLineSegment(sketch, "E20", {"start": v(2715.19, 12.86) * mm, "end": v(2732.19, 12.86) * mm});
            skLineSegment(sketch, "E21", {"start": v(2732.19, 12.86) * mm, "end": v(2732.19, -14.14) * mm});
            skLineSegment(sketch, "E22", {"start": v(2732.19, -14.14) * mm, "end": v(2715.19, -14.14) * mm});
            skLineSegment(sketch, "E23.trimOffspring", {"start": v(2715.19, -14.14) * mm, "end": v(2715.19, -16.14) * mm});
            skSolve(sketch);
        }
        {
            var Q0;
            Q0 = qSketchRegion(id + "F6", true);
            extrude(context, id + "F7", {"entities" : qUnion([Q0]), "operationType" : NewBodyOperationType.ADD, "oppositeDirection" : true, "depth" : 2400 * mm});
        }
        {
            var Q0;
            Q0=makeQuery(id+"F4.opExtrude","SWEPT_BODY",BODY,{"disambiguationData":[OSD([sQuery(id+"F0.wireOp",EDGE,"E0"),sQuery(id+"F0.wireOp",EDGE,"E6.58"),sQuery(id+"F0.wireOp",EDGE,"E7"),sQuery(id+"F1.wireOp",VERTEX,"E10.start"),sQuery(id+"F1.wireOp",EDGE,"E10"),sQuery(id+"F3.wireOp",EDGE,"E11"),sQuery(id+"F3.wireOp",EDGE,"E12"),sQuery(id+"F3.wireOp",EDGE,"E13"),sQuery(id+"F3.wireOp",EDGE,"E14"),sQuery(id+"F3.wireOp",EDGE,"E15"),sQuery(id+"F3.wireOp",EDGE,"E16"),sQuery(id+"F3.wireOp",EDGE,"E17"),sQuery(id+"F3.wireOp",EDGE,"E18")])]});
            var Q1;
            Q1=qCreatedBy(id+"F5.planeOp",FACE);
            mirror(context, id + "F8", {"entities" : qUnion([Q0]), "mirrorPlane" : qUnion([Q1])});
        }
        {
            var Q0;
            Q0=makeQuery(id+"F8.opPattern","COPY",FACE,{"derivedFrom":makeQuery(id+"F7.boolean.opBoolean","MERGE",FACE,{"derivedFrom":[makeQuery(id+"F4.opExtrude","CAP_FACE",FACE,{"disambiguationData":[OSD([sQuery(id+"F0.wireOp",EDGE,"E0"),sQuery(id+"F0.wireOp",EDGE,"E6.58"),sQuery(id+"F0.wireOp",EDGE,"E7"),sQuery(id+"F1.wireOp",VERTEX,"E10.start"),sQuery(id+"F1.wireOp",EDGE,"E10"),sQuery(id+"F3.wireOp",EDGE,"E11"),sQuery(id+"F3.wireOp",EDGE,"E12"),sQuery(id+"F3.wireOp",EDGE,"E13"),sQuery(id+"F3.wireOp",EDGE,"E14"),sQuery(id+"F3.wireOp",EDGE,"E15"),sQuery(id+"F3.wireOp",EDGE,"E16"),sQuery(id+"F3.wireOp",EDGE,"E17"),sQuery(id+"F3.wireOp",EDGE,"E18")])],"isStart":false}),makeQuery(id+"F7.opExtrude","SWEPT_FACE",FACE,{"disambiguationData":[OSD([sQuery(id+"F6.wireOp",EDGE,"E19.left")])]})]}),"instanceName":"1"});
            cPlane(context, id + "F9", {"entities" : qUnion([Q0]), "cplaneType" : CPlaneType.OFFSET, "offset" : 1400 * mm, "oppositeDirection" : true, "width" : 150 * mm, "height" : 150 * mm});
        }
        {
            var Q0;
            Q0=makeQuery(id+"F8.opPattern","COPY",BODY,{"derivedFrom":makeQuery(id+"F4.opExtrude","SWEPT_BODY",BODY,{"disambiguationData":[OSD([sQuery(id+"F0.wireOp",EDGE,"E0"),sQuery(id+"F0.wireOp",EDGE,"E6.58"),sQuery(id+"F0.wireOp",EDGE,"E7"),sQuery(id+"F1.wireOp",VERTEX,"E10.start"),sQuery(id+"F1.wireOp",EDGE,"E10"),sQuery(id+"F3.wireOp",EDGE,"E11"),sQuery(id+"F3.wireOp",EDGE,"E12"),sQuery(id+"F3.wireOp",EDGE,"E13"),sQuery(id+"F3.wireOp",EDGE,"E14"),sQuery(id+"F3.wireOp",EDGE,"E15"),sQuery(id+"F3.wireOp",EDGE,"E16"),sQuery(id+"F3.wireOp",EDGE,"E17"),sQuery(id+"F3.wireOp",EDGE,"E18")])]}),"instanceName":"1"});
            var Q1;
            Q1=qCreatedBy(id+"F9.planeOp",FACE);
            mirror(context, id + "F10", {"entities" : qUnion([Q0]), "mirrorPlane" : qUnion([Q1])});
        }
        {
            var Q0;
            Q0=makeQuery(id+"F8.opPattern","COPY",BODY,{"derivedFrom":makeQuery(id+"F4.opExtrude","SWEPT_BODY",BODY,{"disambiguationData":[OSD([sQuery(id+"F0.wireOp",EDGE,"E0"),sQuery(id+"F0.wireOp",EDGE,"E6.58"),sQuery(id+"F0.wireOp",EDGE,"E7"),sQuery(id+"F1.wireOp",VERTEX,"E10.start"),sQuery(id+"F1.wireOp",EDGE,"E10"),sQuery(id+"F3.wireOp",EDGE,"E11"),sQuery(id+"F3.wireOp",EDGE,"E12"),sQuery(id+"F3.wireOp",EDGE,"E13"),sQuery(id+"F3.wireOp",EDGE,"E14"),sQuery(id+"F3.wireOp",EDGE,"E15"),sQuery(id+"F3.wireOp",EDGE,"E16"),sQuery(id+"F3.wireOp",EDGE,"E17"),sQuery(id+"F3.wireOp",EDGE,"E18")])]}),"instanceName":"1"});
            deleteBodies(context, id + "F11", {"entities" : qUnion([Q0])});
        }
    });
